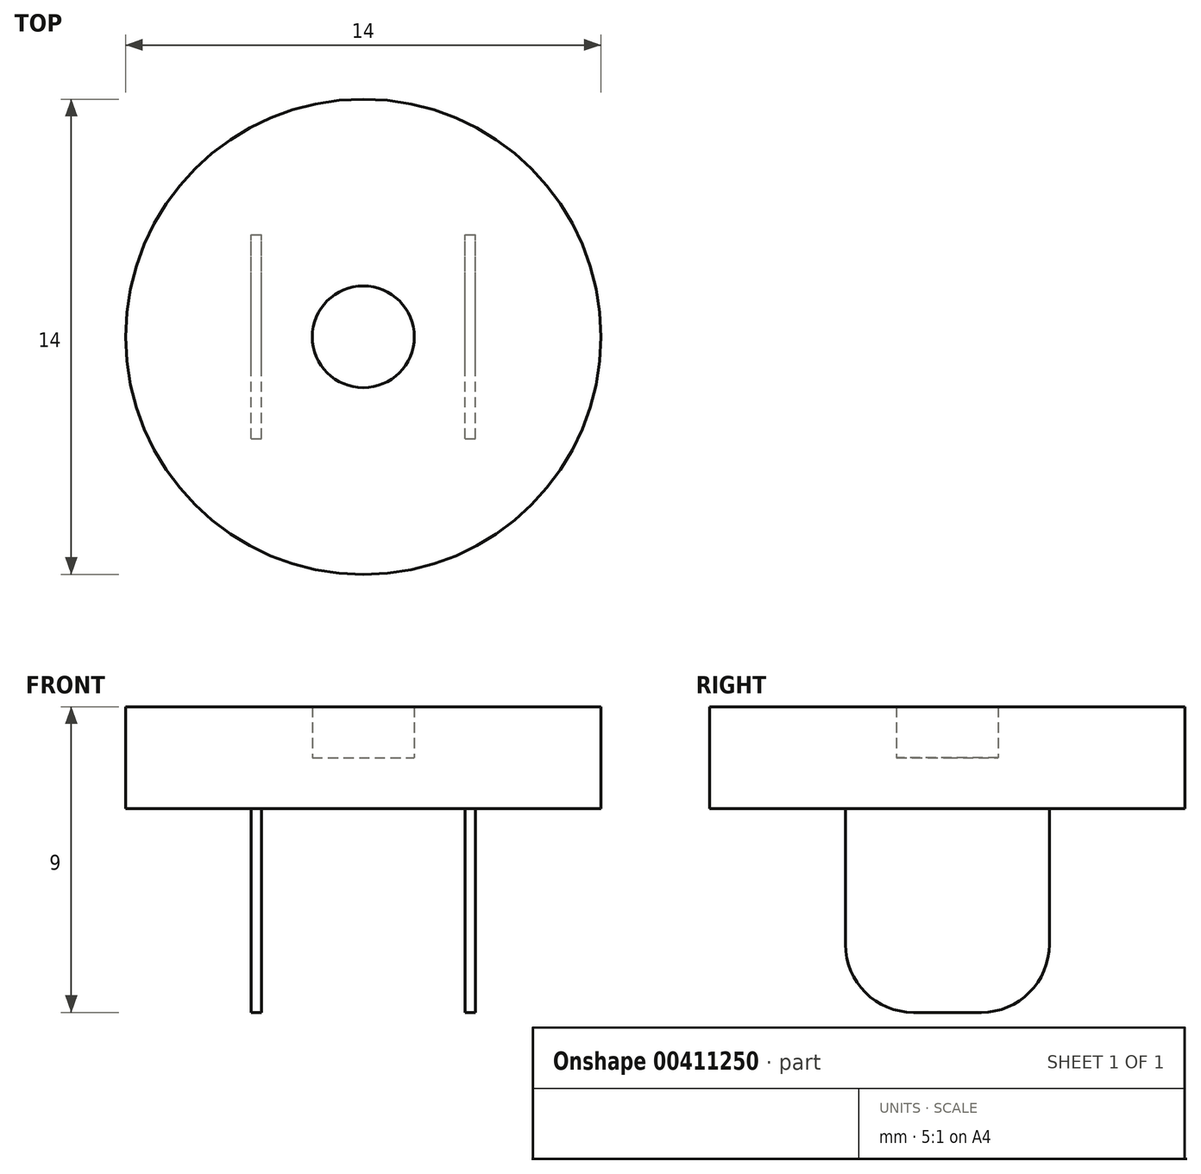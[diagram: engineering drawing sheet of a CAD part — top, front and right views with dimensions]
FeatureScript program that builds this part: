
annotation { "Feature Type Name" : "Feature", "Feature Type Description" : "" }
export const myFeature = defineFeature(function(context is Context, id is Id, definition is map)
    precondition{}
    {
        {
            var Q0;
            Q0=qCreatedBy(makeId("Top.planeOp"),FACE);
            var sketch = newSketch(context, id + "F0", { "sketchPlane" : qUnion([Q0])});
            skCircle(sketch, "E0", {"center": v(0, 0) * mm, "radius": 7 * mm});
            skCircle(sketch, "E1", {"center": v(0, 0) * mm, "radius": 1.5 * mm});
            skSolve(sketch);
        }
        {
            var Q0;
            Q0 = qSketchRegion(id + "F0", true);
            extrude(context, id + "F1", {"entities" : qUnion([Q0]), "depth" : 3 * mm});
        }
        {
            var Q0;
            Q0=makeQuery(id+"F1.opExtrude","CAP_FACE",FACE,{"disambiguationData":[OSD([sQuery(id+"F0.wireOp",EDGE,"E0"),sQuery(id+"F0.wireOp",EDGE,"E1")])],"isStart":true});
            var sketch = newSketch(context, id + "F2", { "sketchPlane" : qUnion([Q0])});
            skCircle(sketch, "E2", {"center": v(0, 0) * mm, "radius": 1.55 * mm});
            skSolve(sketch);
        }
        {
            var Q0;
            Q0 = qSketchRegion(id + "F2", true);
            extrude(context, id + "F3", {"entities" : qUnion([Q0]), "operationType" : NewBodyOperationType.ADD, "oppositeDirection" : true, "depth" : 1.5 * mm});
        }
        {
            var Q0;
            Q0=makeQuery(id+"F3.boolean.opBoolean","MERGE",FACE,{"derivedFrom":[makeQuery(id+"F1.opExtrude","CAP_FACE",FACE,{"disambiguationData":[OSD([sQuery(id+"F0.wireOp",EDGE,"E0"),sQuery(id+"F0.wireOp",EDGE,"E1")])],"isStart":true}),makeQuery(id+"F3.opExtrude","CAP_FACE",FACE,{"disambiguationData":[OSD([sQuery(id+"F2.wireOp",EDGE,"E2")])],"isStart":true})]});
            var sketch = newSketch(context, id + "F4", { "sketchPlane" : qUnion([Q0])});
            skLineSegment(sketch, "E3.bottom", {"start": v(-3.3, 3) * mm, "end": v(-3, 3) * mm});
            skLineSegment(sketch, "E3.top", {"start": v(-3.3, -3) * mm, "end": v(-3, -3) * mm});
            skLineSegment(sketch, "E3.left", {"start": v(-3.3, 3) * mm, "end": v(-3.3, -3) * mm});
            skLineSegment(sketch, "E3.right", {"start": v(-3, 3) * mm, "end": v(-3, -3) * mm});
            skLineSegment(sketch, "E4.bottom", {"start": v(3, 3) * mm, "end": v(3.3, 3) * mm});
            skLineSegment(sketch, "E4.top", {"start": v(3, -3) * mm, "end": v(3.3, -3) * mm});
            skLineSegment(sketch, "E4.left", {"start": v(3, 3) * mm, "end": v(3, -3) * mm});
            skLineSegment(sketch, "E4.right", {"start": v(3.3, 3) * mm, "end": v(3.3, -3) * mm});
            skSolve(sketch);
        }
        {
            var Q0;
            Q0 = qSketchRegion(id + "F4", true);
            extrude(context, id + "F5", {"entities" : qUnion([Q0]), "operationType" : NewBodyOperationType.ADD, "depth" : 6 * mm});
        }
        {
            var Q0;
            Q0=makeQuery(id+"F5.opExtrude","CAP_EDGE",EDGE,{"disambiguationData":[OSD([sQuery(id+"F4.wireOp",EDGE,"E3.bottom")])],"isStart":false});
            var Q1;
            Q1=makeQuery(id+"F5.opExtrude","CAP_EDGE",EDGE,{"disambiguationData":[OSD([sQuery(id+"F4.wireOp",EDGE,"E3.top")])],"isStart":false});
            var Q2;
            Q2=makeQuery(id+"F5.opExtrude","CAP_EDGE",EDGE,{"disambiguationData":[OSD([sQuery(id+"F4.wireOp",EDGE,"E4.top")])],"isStart":false});
            var Q3;
            Q3=makeQuery(id+"F5.opExtrude","CAP_EDGE",EDGE,{"disambiguationData":[OSD([sQuery(id+"F4.wireOp",EDGE,"E4.bottom")])],"isStart":false});
            fillet(context, id + "F6", {"entities" : qUnion([Q0, Q1, Q2, Q3]), "radius" : 2 * mm, "tangentPropagation" : true, "allowEdgeOverflow" : false});
        }
    });
